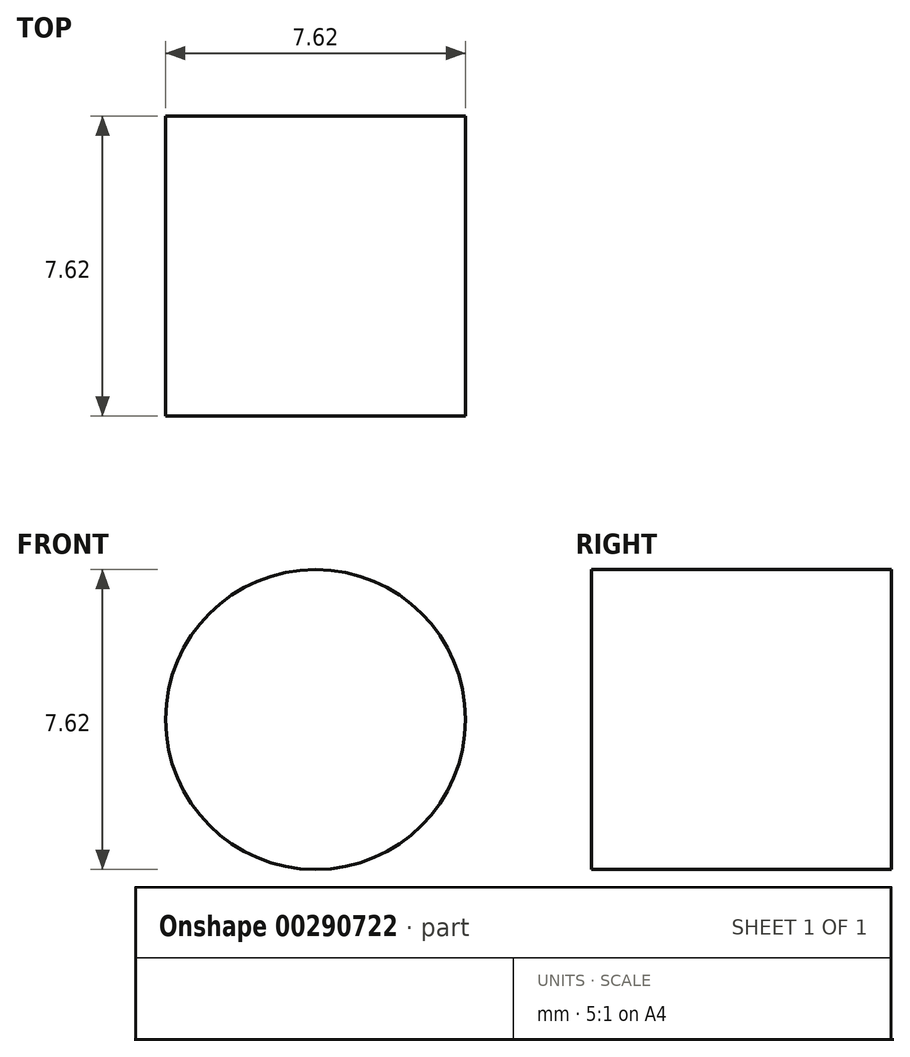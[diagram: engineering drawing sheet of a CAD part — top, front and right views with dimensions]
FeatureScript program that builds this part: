
annotation { "Feature Type Name" : "Feature", "Feature Type Description" : "" }
export const myFeature = defineFeature(function(context is Context, id is Id, definition is map)
    precondition{}
    {
        {
            var Q0;
            Q0=qCreatedBy(makeId("Front.planeOp"),FACE);
            var sketch = newSketch(context, id + "F0", { "sketchPlane" : qUnion([Q0])});
            skCircle(sketch, "E0", {"center": v(0, 0) * mm, "radius": 3.81 * mm});
            skSolve(sketch);
        }
        {
            var Q0;
            Q0 = qSketchRegion(id + "F0", true);
            extrude(context, id + "F1", {"entities" : qUnion([Q0]), "depth" : 7.62 * mm});
        }
    });
